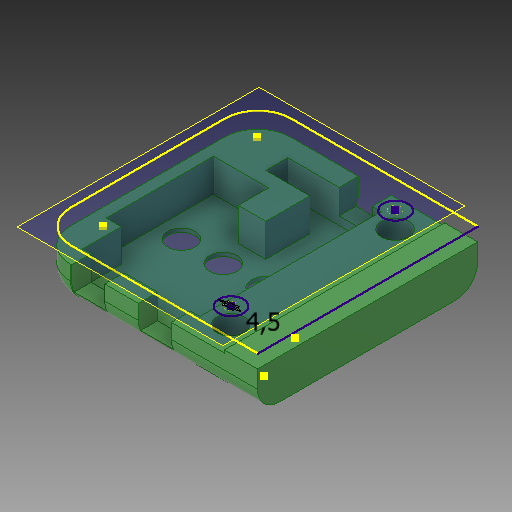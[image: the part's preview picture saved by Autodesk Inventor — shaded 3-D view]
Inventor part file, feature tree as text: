
AUTODESK INVENTOR PART (.ipt)
format: ipt  version: 2018 (Build 220112000, 112)  size: 303,104 bytes
history: native  units: mm
features: reference x11, sketch x6, extrude x5, plane x3, other x3, fillet x2, chamfer x1, direct_edit x1, move_body x1
ambient origin geometry x8: Origin, YZ Plane, XZ Plane, XY Plane, X Axis, Y Axis, Z Axis, Center Point
bodies: Solid1 (feature_tree)
feature tree (33):
  extrude  "Extrusion1"  Depth=40.0mm
  sketch  "Sketch2"  dims[d2=4.0mm d3=0.0mm d4=40.0mm]
  plane  "Work Plane1"
  extrude  "Extrusion2"  Depth=40.0mm
  extrude  "Extrusion3"  Depth=5.0mm
  sketch  "Sketch3"  dims[d5=40.0mm d6=5.0mm]
  extrude  "Extrusion4"  Depth=21.4mm
  plane  "Work Plane2"
  fillet  "Fillet4"  Radius=2.0mm
  fillet  "Fillet5"  Radius=9.0mm
  extrude  "Extrusion6"  Depth=24.0mm
  chamfer  "Chamfer3"  Distance=7.62mm
  direct_edit  "Direct Edit3"
  plane  "Work Plane3"
  sketch  "Sketch8"  dims[d13=7.62mm d14=7.62mm d15=9.0mm d16=12.0mm d17=9.0mm d18=12.0mm d19=9.0mm d20=12.0mm d21=3.3mm d22=10.0mm d23=0.0mm d24=6.0mm d25=0.0mm d40=6.0mm d41=10.0mm d42=6.0mm d43=10.0mm d44=6.0mm d45=10.0mm d46=4.5mm d47=0.0mm d61=8.0mm d62=4.0mm d63=2.7mm d64=5.0mm d65=10.0mm d66=5.5mm d67=6.0mm d68=4.0mm d70=5.0mm d71=0.0mm d72=0.0mm d73=2.0mm d74=2.0mm d75=45.0deg d76=0.0mm d77=0.0mm d78=-3.5mm d79=4.5mm]
  sketch  "Sketch1"  dims[d0=6.0mm d1=40.0mm]
  sketch  "Sketch4"  dims[d7=20.0mm d8=21.4mm d9=2.0mm d10=9.0mm]
  sketch  "Sketch7"  dims[d11=4.5mm d12=24.0mm]
  reference  "Reference3"
  reference  "Reference4"
  reference  "Reference5"
  reference  "Reference6"
  reference  "Reference7"
  reference  "Reference8"
  reference  "Reference9"
  reference  "Reference10"
  reference  "Reference11"
  reference  "Reference12"
  reference  "Reference13"
  other  "<userpath>\Dropbox\Skola\Projekt\Kretsn_Brillz_V2\3D\Main.iam"
  other  "Main.iam"
  other  "Holster_Bottom:1"
  move_body  "Move4"
